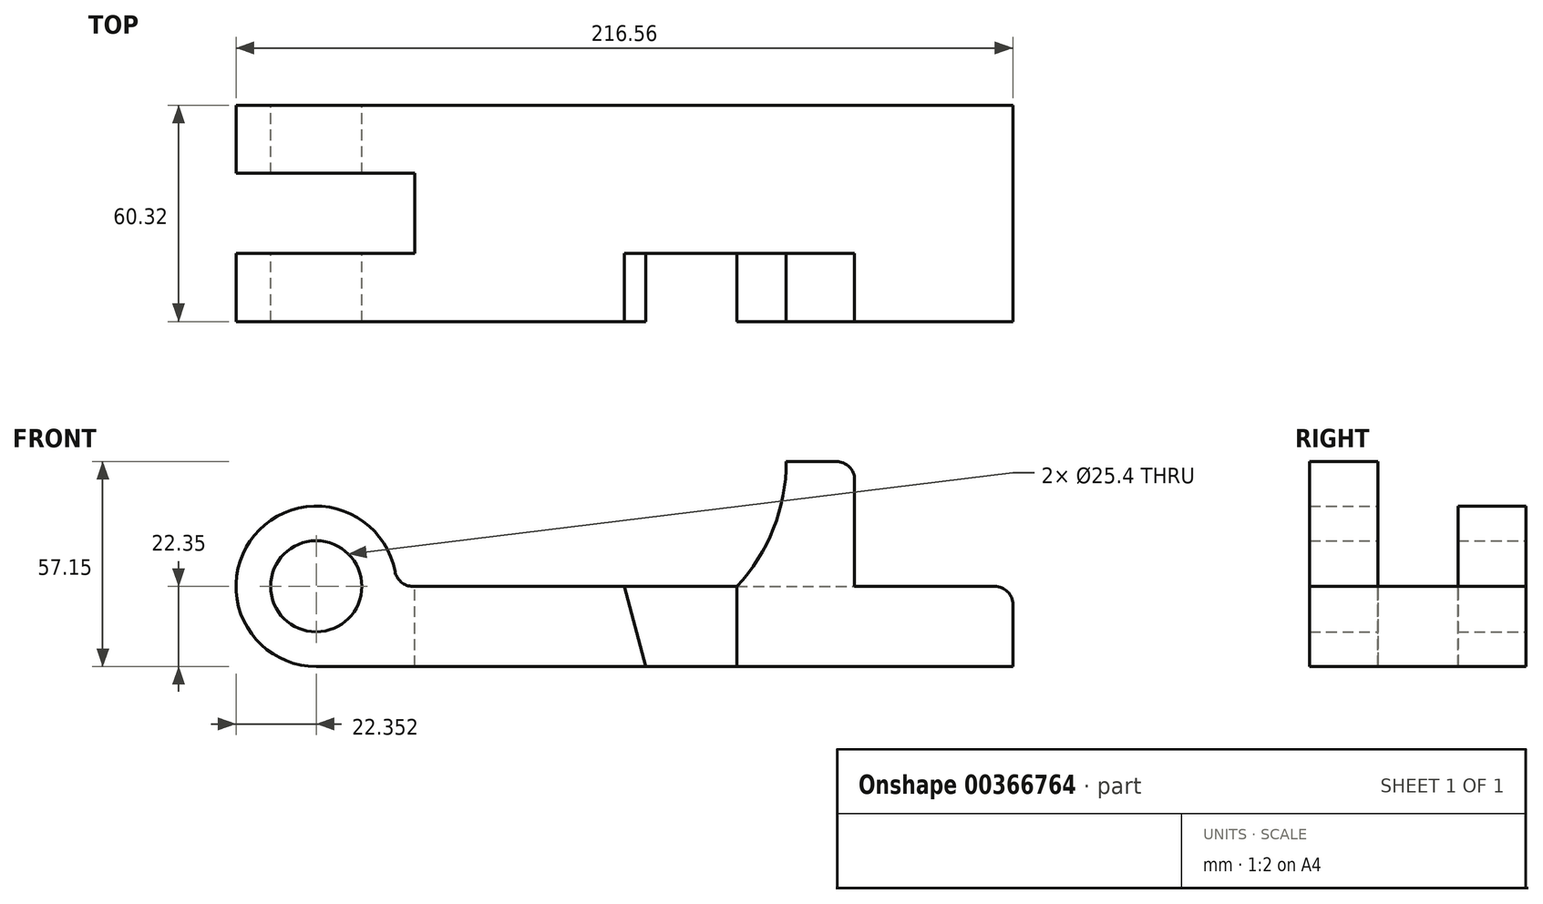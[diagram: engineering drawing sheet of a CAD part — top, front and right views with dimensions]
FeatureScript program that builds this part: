
annotation { "Feature Type Name" : "Feature", "Feature Type Description" : "" }
export const myFeature = defineFeature(function(context is Context, id is Id, definition is map)
    precondition{}
    {
        {
            var Q0;
            Q0=qCreatedBy(makeId("Front.planeOp"),FACE);
            var sketch = newSketch(context, id + "F0", { "sketchPlane" : qUnion([Q0])});
            skArc(sketch, "E0", {"start": v(-63.58, 0) * mm, "mid": v(-101.73, 15.8) * mm, "end": v(-85.93, -22.35) * mm});
            skCircle(sketch, "E1", {"center": v(-85.93, 0) * mm, "radius": 12.7 * mm});
            skLineSegment(sketch, "E2.bottom", {"start": v(-85.93, -22.35) * mm, "end": v(108.28, -22.35) * mm});
            skLineSegment(sketch, "E2.right", {"start": v(108.28, -22.35) * mm, "end": v(108.28, 0) * mm});
            skLineSegment(sketch, "E3.trimOffspring", {"start": v(-63.58, 0) * mm, "end": v(108.28, 0) * mm});
            skSolve(sketch);
        }
        {
            var Q0;
            Q0=makeQuery(id+"F0.imprint","IMPRINT",FACE,{"disambiguationData":[TD([[makeQuery(id+"F0.imprint","IMPRINT",EDGE,{"derivedFrom":sQuery(id+"F0.wireOp",EDGE,"E0")}),1.0]])]});
            extrude(context, id + "F1", {"entities" : qUnion([Q0]), "endBound" : BoundingType.SYMMETRIC, "depth" : 60.32 * mm});
        }
        {
            var Q0;
            Q0=makeQuery(id+"F1.opExtrude","SWEPT_FACE",FACE,{"disambiguationData":[OSD([sQuery(id+"F0.wireOp",EDGE,"E3.trimOffspring")])]});
            var sketch = newSketch(context, id + "F2", { "sketchPlane" : qUnion([Q0])});
            skLineSegment(sketch, "E4.bottom", {"start": v(-129.56, 11.16) * mm, "end": v(-58.5, 11.16) * mm});
            skLineSegment(sketch, "E4.top", {"start": v(-129.56, -11.16) * mm, "end": v(-58.5, -11.16) * mm});
            skLineSegment(sketch, "E4.left", {"start": v(-129.56, 11.16) * mm, "end": v(-129.56, -11.16) * mm});
            skLineSegment(sketch, "E4.right", {"start": v(-58.5, 11.16) * mm, "end": v(-58.5, -11.16) * mm});
            skSolve(sketch);
        }
        {
            var Q0;
            {var subQ0=sQuery(id+"F2.wireOp",EDGE,"E4.right");Q0=makeQuery(id+"F2.imprint","IMPRINT",FACE,{"disambiguationData":[TD([[makeQuery(id+"F2.imprint","IMPRINT",EDGE,{"derivedFrom":subQ0}),-1.0]])]});}
            var Q1;
            {var subQ0=sQuery(id+"F2.wireOp",EDGE,"E4.left");Q1=makeQuery(id+"F2.imprint","IMPRINT",FACE,{"disambiguationData":[TD([[makeQuery(id+"F2.imprint","IMPRINT",EDGE,{"derivedFrom":subQ0}),1.0]])]});}
            extrude(context, id + "F3", {"entities" : qUnion([Q0, Q1]), "operationType" : NewBodyOperationType.REMOVE, "endBound" : BoundingType.SYMMETRIC, "oppositeDirection" : true, "depth" : 508 * mm});
        }
        {
            var Q0;
            Q0=makeQuery(id+"F1.opExtrude","CAP_FACE",FACE,{"disambiguationData":[OSD([sQuery(id+"F0.wireOp",EDGE,"E0"),sQuery(id+"F0.wireOp",EDGE,"E1"),sQuery(id+"F0.wireOp",EDGE,"E2.bottom"),sQuery(id+"F0.wireOp",EDGE,"E2.right"),sQuery(id+"F0.wireOp",EDGE,"E3.trimOffspring")])],"isStart":false});
            var sketch = newSketch(context, id + "F4", { "sketchPlane" : qUnion([Q0])});
            skLineSegment(sketch, "E5", {"start": v(-0.08, 0) * mm, "end": v(5.92, -22.35) * mm});
            skLineSegment(sketch, "E6", {"start": v(5.92, -22.35) * mm, "end": v(31.32, -22.35) * mm});
            skLineSegment(sketch, "E7", {"start": v(31.32, -22.35) * mm, "end": v(31.32, 0) * mm});
            skLineSegment(sketch, "E8", {"start": v(31.32, 0) * mm, "end": v(-0.08, 0) * mm});
            skCircle(sketch, "E9.0", {"center": v(-85.93, 0) * mm, "radius": 12.7 * mm});
            skSolve(sketch);
        }
        {
            var Q0;
            Q0=makeQuery(id+"F4.imprint","IMPRINT",FACE,{"disambiguationData":[TD([[makeQuery(id+"F4.imprint","IMPRINT",EDGE,{"derivedFrom":sQuery(id+"F4.wireOp",EDGE,"E5")}),1.0]])]});
            extrude(context, id + "F5", {"entities" : qUnion([Q0]), "operationType" : NewBodyOperationType.REMOVE, "oppositeDirection" : true, "depth" : 19.05 * mm});
        }
        {
            var Q0;
            {var subQ0=sQuery(id+"F0.wireOp",EDGE,"E2.bottom");var subQ1=sQuery(id+"F0.wireOp",EDGE,"E2.right");var subQ2=sQuery(id+"F0.wireOp",EDGE,"E3.trimOffspring");Q0=makeQuery(id+"F5.boolean.opBoolean","SPLIT",FACE,{"disambiguationData":[TD([makeQuery(id+"F1.opExtrude","SWEPT_FACE",FACE,{"disambiguationData":[OSD([subQ1])]})])],"derivedFrom":makeQuery(id+"F1.opExtrude","CAP_FACE",FACE,{"disambiguationData":[OSD([sQuery(id+"F0.wireOp",EDGE,"E0"),sQuery(id+"F0.wireOp",EDGE,"E1"),subQ0,subQ1,subQ2])],"isStart":false})});}
            var sketch = newSketch(context, id + "F6", { "sketchPlane" : qUnion([Q0])});
            skLineSegment(sketch, "E10.top", {"start": v(59.08, 34.8) * mm, "end": v(45.11, 34.8) * mm});
            skLineSegment(sketch, "E10.left", {"start": v(64.16, 0) * mm, "end": v(64.16, 29.72) * mm});
            skArc(sketch, "E11", {"start": v(31.32, 0) * mm, "mid": v(41.54, 16.08) * mm, "end": v(45.11, 34.8) * mm});
            skLineSegment(sketch, "E12", {"start": v(64.16, 0) * mm, "end": v(31.32, 0) * mm});
            skCircle(sketch, "E13.0", {"center": v(-85.93, 0) * mm, "radius": 12.7 * mm});
            skPoint(sketch, "E14.visualSharp", {"position": v(64.16, 34.8) * mm});
            skArc(sketch, "E14.filletArc", {"start": v(64.16, 29.72) * mm, "mid": v(62.67, 33.31) * mm, "end": v(59.08, 34.8) * mm});
            skSolve(sketch);
        }
        {
            var Q0;
            Q0=makeQuery(id+"F6.imprint","IMPRINT",FACE,{"disambiguationData":[TD([[makeQuery(id+"F6.imprint","IMPRINT",EDGE,{"derivedFrom":sQuery(id+"F6.wireOp",EDGE,"E10.top")}),1.0]])]});
            extrude(context, id + "F7", {"entities" : qUnion([Q0]), "operationType" : NewBodyOperationType.ADD, "oppositeDirection" : true, "depth" : 19.05 * mm});
        }
        {
            var Q0;
            {var subQ0=sQuery(id+"F0.wireOp",EDGE,"E0");var subQ1=sQuery(id+"F0.wireOp",EDGE,"E3.trimOffspring");Q0=makeQuery(id+"F3.boolean.opBoolean","SPLIT",EDGE,{"disambiguationData":[TD([makeQuery(id+"F3.opExtrude","SWEPT_FACE",FACE,{"disambiguationData":[OSD([sQuery(id+"F2.wireOp",EDGE,"E4.top")])]})])],"derivedFrom":makeQuery(id+"F1.opExtrude","SWEPT_EDGE",EDGE,{"disambiguationData":[OSD([subQ0,subQ1])]})});}
            var Q1;
            {var subQ0=sQuery(id+"F0.wireOp",EDGE,"E0");var subQ1=sQuery(id+"F0.wireOp",EDGE,"E3.trimOffspring");Q1=makeQuery(id+"F3.boolean.opBoolean","SPLIT",EDGE,{"disambiguationData":[TD([makeQuery(id+"F3.opExtrude","SWEPT_FACE",FACE,{"disambiguationData":[OSD([sQuery(id+"F2.wireOp",EDGE,"E4.bottom")])]})])],"derivedFrom":makeQuery(id+"F1.opExtrude","SWEPT_EDGE",EDGE,{"disambiguationData":[OSD([subQ0,subQ1])]})});}
            var Q2;
            Q2=makeQuery(id+"F1.opExtrude","SWEPT_EDGE",EDGE,{"disambiguationData":[OSD([sQuery(id+"F0.wireOp",EDGE,"E2.right"),sQuery(id+"F0.wireOp",EDGE,"E3.trimOffspring")])]});
            fillet(context, id + "F8", {"entities" : qUnion([Q0, Q1, Q2]), "radius" : 5.08 * mm, "tangentPropagation" : true, "allowEdgeOverflow" : false});
        }
    });
